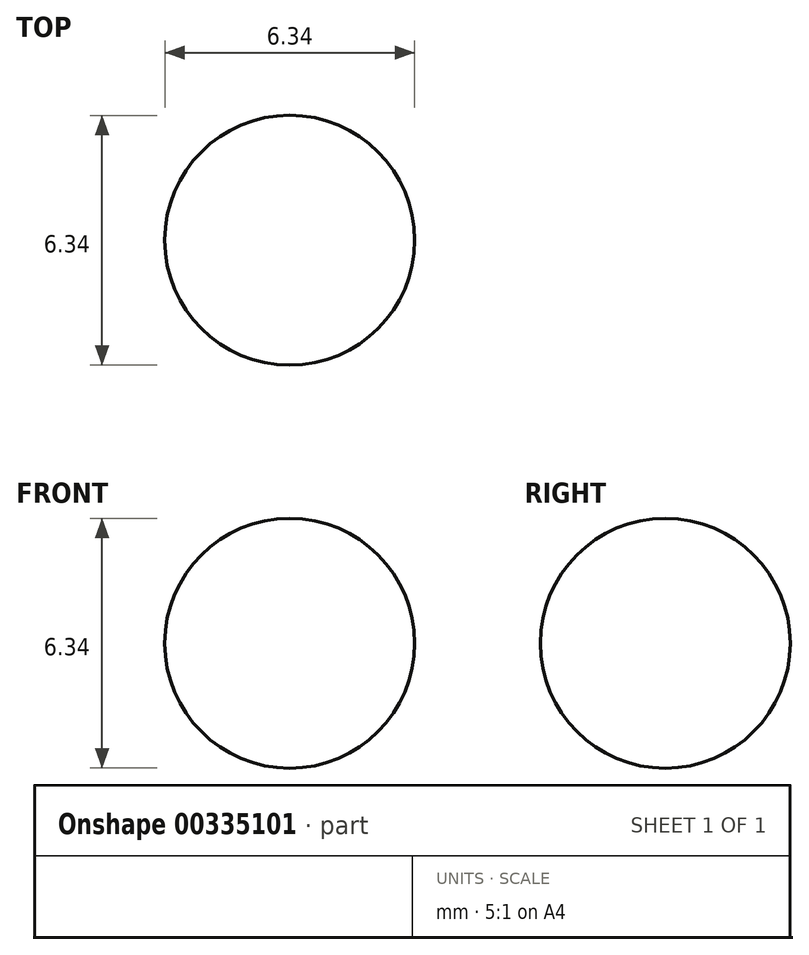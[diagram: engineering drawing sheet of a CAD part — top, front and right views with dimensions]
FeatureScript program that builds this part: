
annotation { "Feature Type Name" : "Feature", "Feature Type Description" : "" }
export const myFeature = defineFeature(function(context is Context, id is Id, definition is map)
    precondition{}
    {
        {
            var Q0;
            Q0=qCreatedBy(makeId("Front.planeOp"),FACE);
            var sketch = newSketch(context, id + "F0", { "sketchPlane" : qUnion([Q0])});
            skCircle(sketch, "E0", {"center": v(0, 0) * mm, "radius": 3.18 * mm});
            skLineSegment(sketch, "E1", {"start": v(0, 3.18) * mm, "end": v(0, -3.18) * mm});
            skSolve(sketch);
        }
        {
            var Q0;
            {var subQ0=sQuery(id+"F0.wireOp",EDGE,"E1");Q0=makeQuery(id+"F0.imprint","IMPRINT",FACE,{"disambiguationData":[TD([[makeQuery(id+"F0.imprint","IMPRINT",EDGE,{"derivedFrom":subQ0}),1.0]])]});}
            var Q1;
            Q1=sQuery(id+"F0.wireOp",EDGE,"E1");
            revolve(context, id + "F1", {"entities" : qUnion([Q0]), "axis" : qUnion([Q1]), "revolveType" : RevolveType.FULL});
        }
    });
